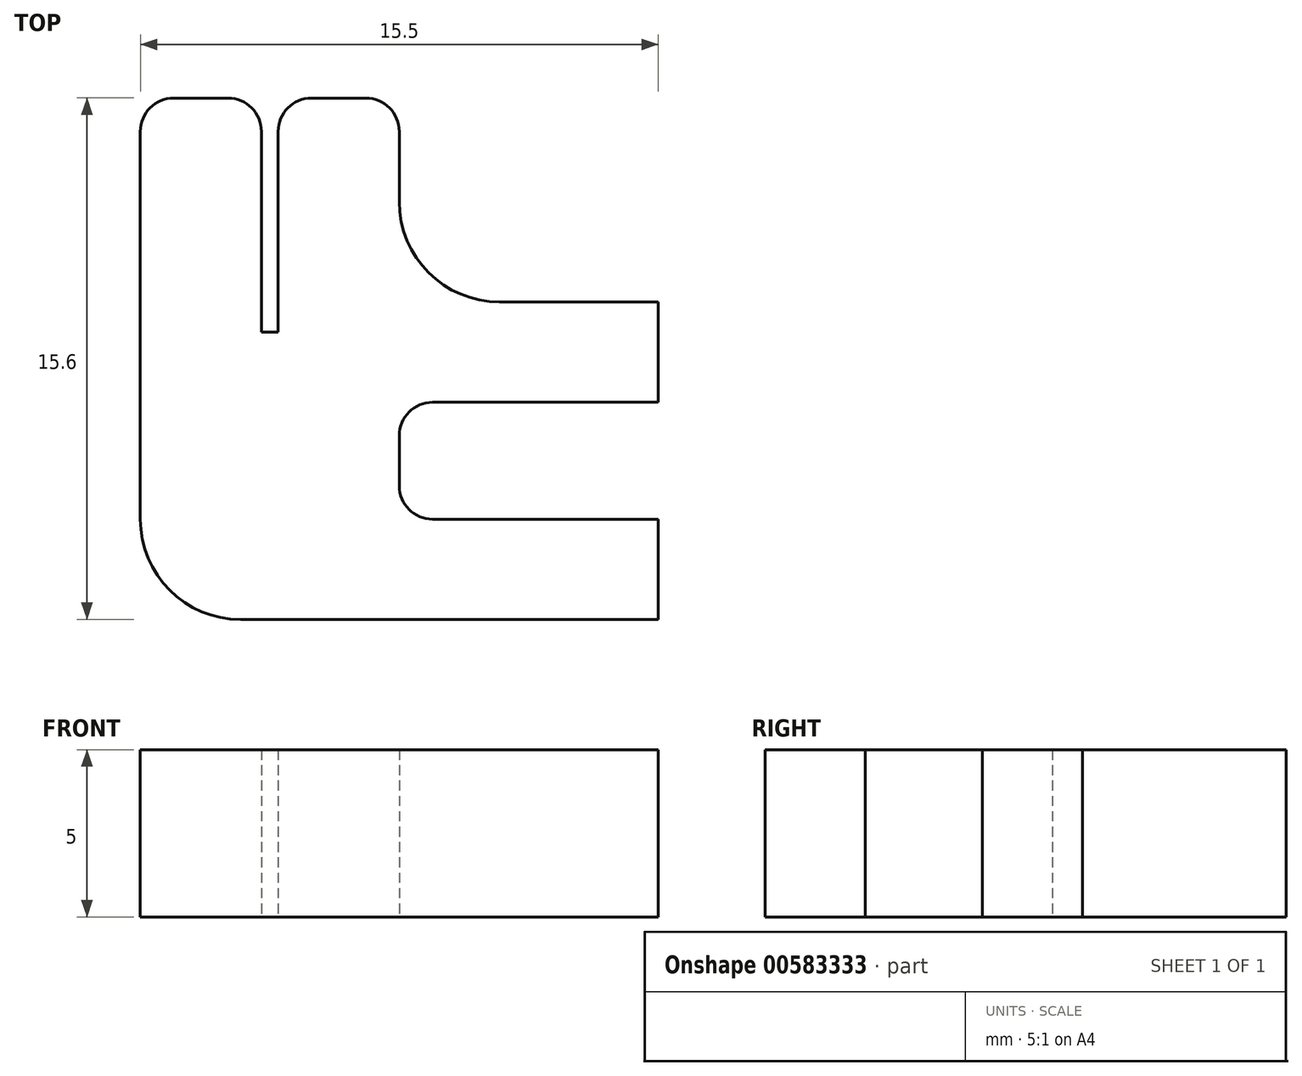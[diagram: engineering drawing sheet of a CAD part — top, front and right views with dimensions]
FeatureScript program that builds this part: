
annotation { "Feature Type Name" : "Feature", "Feature Type Description" : "" }
export const myFeature = defineFeature(function(context is Context, id is Id, definition is map)
    precondition{}
    {
        {
            var Q0;
            Q0=qCreatedBy(makeId("Top.planeOp"),FACE);
            var sketch = newSketch(context, id + "F0", { "sketchPlane" : qUnion([Q0])});
            skLineSegment(sketch, "E0.bottom", {"start": v(-36, 42.24) * mm, "end": v(-34.37, 42.24) * mm});
            skLineSegment(sketch, "E0.top", {"start": v(-34, 26.64) * mm, "end": v(-21.5, 26.64) * mm});
            skLineSegment(sketch, "E0.left", {"start": v(-37, 41.24) * mm, "end": v(-37, 29.64) * mm});
            skLineSegment(sketch, "E0.right", {"start": v(-21.5, 36.14) * mm, "end": v(-21.5, 33.14) * mm});
            skPoint(sketch, "E1.visualSharp", {"position": v(-37, 26.64) * mm});
            skArc(sketch, "E1.filletArc", {"start": v(-37, 29.64) * mm, "mid": v(-36.11, 27.51) * mm, "end": v(-34, 26.64) * mm});
            skLineSegment(sketch, "E2", {"start": v(-21.5, 26.64) * mm, "end": v(-21.5, 29.64) * mm});
            skLineSegment(sketch, "E3", {"start": v(-21.5, 29.64) * mm, "end": v(-28.24, 29.64) * mm});
            skLineSegment(sketch, "E4", {"start": v(-21.5, 33.14) * mm, "end": v(-28.24, 33.14) * mm});
            skLineSegment(sketch, "E5", {"start": v(-29.24, 32.14) * mm, "end": v(-29.24, 30.64) * mm});
            skPoint(sketch, "E6.orphan", {"position": v(-37, 33.14) * mm});
            skLineSegment(sketch, "E7", {"start": v(-29.24, 39.14) * mm, "end": v(-29.24, 41.24) * mm});
            skLineSegment(sketch, "E8", {"start": v(-21.5, 33.14) * mm, "end": v(-21.5, 36.14) * mm});
            skLineSegment(sketch, "E9", {"start": v(-21.5, 36.14) * mm, "end": v(-26.24, 36.14) * mm});
            skPoint(sketch, "E10.visualSharp", {"position": v(-29.24, 36.14) * mm});
            skArc(sketch, "E10.filletArc", {"start": v(-29.24, 39.14) * mm, "mid": v(-28.36, 37.01) * mm, "end": v(-26.24, 36.14) * mm});
            skPoint(sketch, "E11.visualSharp", {"position": v(-29.24, 33.14) * mm});
            skArc(sketch, "E11.filletArc", {"start": v(-28.24, 33.14) * mm, "mid": v(-28.95, 32.84) * mm, "end": v(-29.24, 32.14) * mm});
            skPoint(sketch, "E12.visualSharp", {"position": v(-29.24, 29.64) * mm});
            skArc(sketch, "E12.filletArc", {"start": v(-29.24, 30.64) * mm, "mid": v(-28.95, 29.93) * mm, "end": v(-28.24, 29.64) * mm});
            skLineSegment(sketch, "E13.trimOffspring", {"start": v(-21.5, 29.64) * mm, "end": v(-21.5, 26.64) * mm});
            skPoint(sketch, "E14.orphan", {"position": v(-21.5, 42.24) * mm});
            skLineSegment(sketch, "E15.top", {"start": v(-33.37, 35.24) * mm, "end": v(-32.87, 35.24) * mm});
            skLineSegment(sketch, "E15.left", {"start": v(-33.37, 41.24) * mm, "end": v(-33.37, 35.24) * mm});
            skLineSegment(sketch, "E15.right", {"start": v(-32.87, 41.24) * mm, "end": v(-32.87, 35.24) * mm});
            skLineSegment(sketch, "E16.trimOffspring", {"start": v(-31.87, 42.24) * mm, "end": v(-30.24, 42.24) * mm});
            skPoint(sketch, "E17.end.orphan", {"position": v(-32.87, 42.24) * mm});
            skPoint(sketch, "E18.visualSharp", {"position": v(-33.37, 42.24) * mm});
            skArc(sketch, "E18.filletArc", {"start": v(-33.37, 41.24) * mm, "mid": v(-33.66, 41.94) * mm, "end": v(-34.37, 42.24) * mm});
            skArc(sketch, "E19.filletArc", {"start": v(-31.87, 42.24) * mm, "mid": v(-32.58, 41.94) * mm, "end": v(-32.87, 41.24) * mm});
            skPoint(sketch, "E20.visualSharp", {"position": v(-29.24, 42.24) * mm});
            skArc(sketch, "E20.filletArc", {"start": v(-29.24, 41.24) * mm, "mid": v(-29.54, 41.94) * mm, "end": v(-30.24, 42.24) * mm});
            skPoint(sketch, "E21.visualSharp", {"position": v(-37, 42.24) * mm});
            skArc(sketch, "E21.filletArc", {"start": v(-36, 42.24) * mm, "mid": v(-36.7, 41.94) * mm, "end": v(-37, 41.24) * mm});
            skSolve(sketch);
        }
        {
            var Q0;
            Q0=makeQuery(id+"F0.imprint","IMPRINT",FACE,{"disambiguationData":[TD([[makeQuery(id+"F0.imprint","IMPRINT",EDGE,{"derivedFrom":sQuery(id+"F0.wireOp",EDGE,"E0.bottom")}),-1.0]])]});
            extrude(context, id + "F1", {"entities" : qUnion([Q0]), "depth" : 5 * mm, "offsetDistance" : 25 * mm});
        }
    });
